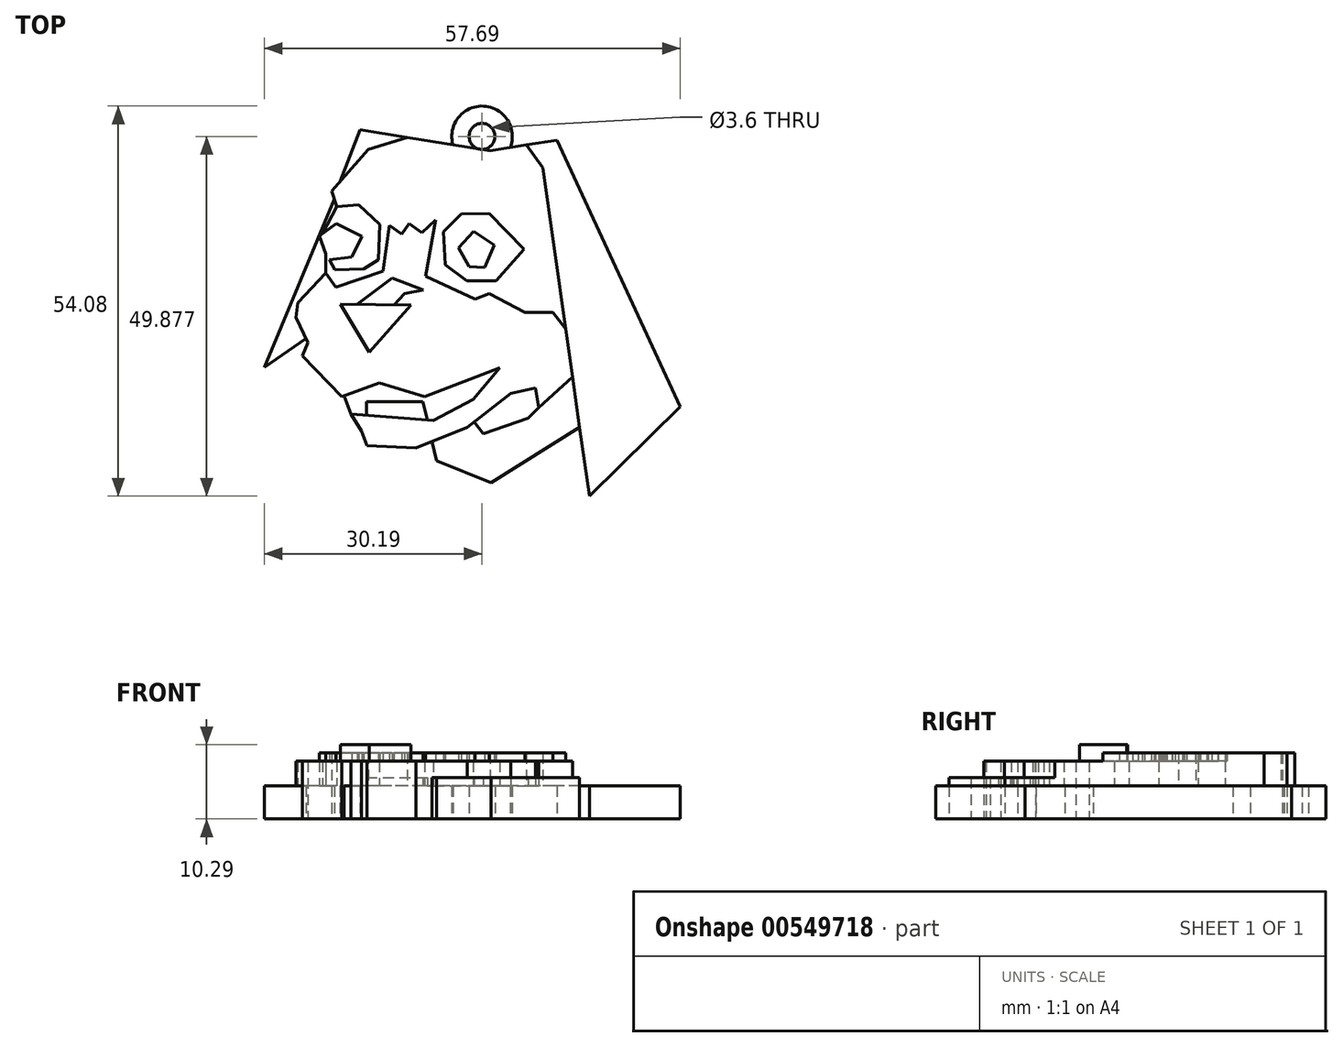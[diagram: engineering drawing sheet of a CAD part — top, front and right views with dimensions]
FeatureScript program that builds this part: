
annotation { "Feature Type Name" : "Feature", "Feature Type Description" : "" }
export const myFeature = defineFeature(function(context is Context, id is Id, definition is map)
    precondition{}
    {
        {
            var Q0;
            Q0=qCreatedBy(makeId("Top.planeOp"),FACE);
            var sketch = newSketch(context, id + "F0", { "sketchPlane" : qUnion([Q0])});
            skLineSegment(sketch, "E0", {"start": v(-28.92, 19.78) * mm, "end": v(-27.96, 16.71) * mm});
            skLineSegment(sketch, "E1", {"start": v(-27.96, 16.71) * mm, "end": v(-23.77, 17.1) * mm});
            skLineSegment(sketch, "E2", {"start": v(-23.77, 17.1) * mm, "end": v(-19.66, 13.35) * mm});
            skLineSegment(sketch, "E3", {"start": v(-19.66, 13.35) * mm, "end": v(-19.93, 6.56) * mm});
            skLineSegment(sketch, "E4", {"start": v(-19.93, 6.56) * mm, "end": v(-22.81, 4.73) * mm});
            skLineSegment(sketch, "E5", {"start": v(-22.81, 4.73) * mm, "end": v(-28.35, 4.56) * mm});
            skLineSegment(sketch, "E6", {"start": v(-28.35, 4.56) * mm, "end": v(-30.1, 7.71) * mm});
            skLineSegment(sketch, "E7", {"start": v(-30.1, 7.71) * mm, "end": v(-30.1, 3.95) * mm});
            skLineSegment(sketch, "E8", {"start": v(-30.1, 7.71) * mm, "end": v(-31.36, 11.09) * mm});
            skLineSegment(sketch, "E9", {"start": v(-31.36, 11.09) * mm, "end": v(-28.1, 13.47) * mm});
            skLineSegment(sketch, "E10", {"start": v(-28.1, 13.47) * mm, "end": v(-23.11, 10.99) * mm});
            skLineSegment(sketch, "E11", {"start": v(-23.11, 10.99) * mm, "end": v(-25.06, 7.08) * mm});
            skLineSegment(sketch, "E12", {"start": v(-25.06, 7.08) * mm, "end": v(-29.42, 6.49) * mm});
            skLineSegment(sketch, "E13", {"start": v(-27.96, 16.71) * mm, "end": v(-30.7, 11.57) * mm});
            skLineSegment(sketch, "E14", {"start": v(-28.44, 18.25) * mm, "end": v(-41.92, -14.16) * mm});
            skLineSegment(sketch, "E15", {"start": v(-41.92, -14.16) * mm, "end": v(-33.9, -8.63) * mm});
            skLineSegment(sketch, "E16", {"start": v(-33.9, -8.63) * mm, "end": v(-35.81, -4.56) * mm});
            skLineSegment(sketch, "E17", {"start": v(-35.81, -4.56) * mm, "end": v(-35.46, -1.8) * mm});
            skLineSegment(sketch, "E18", {"start": v(-35.46, -1.8) * mm, "end": v(-30.1, 3.95) * mm});
            skLineSegment(sketch, "E19", {"start": v(-30.1, 3.95) * mm, "end": v(-28.12, 1.24) * mm});
            skLineSegment(sketch, "E20", {"start": v(-28.12, 1.24) * mm, "end": v(-19.08, 4.3) * mm});
            skLineSegment(sketch, "E21", {"start": v(-19.08, 4.3) * mm, "end": v(-17.81, 13.18) * mm});
            skLineSegment(sketch, "E22", {"start": v(-17.81, 13.18) * mm, "end": v(-15.44, 11.49) * mm});
            skLineSegment(sketch, "E23", {"start": v(-15.44, 11.49) * mm, "end": v(-14, 13.5) * mm});
            skLineSegment(sketch, "E24", {"start": v(-14, 13.5) * mm, "end": v(-11.55, 11.76) * mm});
            skLineSegment(sketch, "E25", {"start": v(-11.55, 11.76) * mm, "end": v(-8.94, 14.17) * mm});
            skLineSegment(sketch, "E26", {"start": v(-8.94, 14.17) * mm, "end": v(-10.88, 3.37) * mm});
            skLineSegment(sketch, "E27", {"start": v(-10.88, 3.37) * mm, "end": v(-1.34, -1.04) * mm});
            skLineSegment(sketch, "E28", {"start": v(-1.34, -1.04) * mm, "end": v(1.4, 0) * mm});
            skLineSegment(sketch, "E29", {"start": v(1.4, 0) * mm, "end": v(8.24, -3.6) * mm});
            skLineSegment(sketch, "E30", {"start": v(8.24, -3.6) * mm, "end": v(13.64, -3.6) * mm});
            skLineSegment(sketch, "E31", {"start": v(13.64, -3.6) * mm, "end": v(16.12, -6.8) * mm});
            skLineSegment(sketch, "E32", {"start": v(11.71, 24.26) * mm, "end": v(20.68, -38.98) * mm});
            skLineSegment(sketch, "E33", {"start": v(20.68, -38.98) * mm, "end": v(38.19, -21.8) * mm});
            skLineSegment(sketch, "E34", {"start": v(38.19, -21.8) * mm, "end": v(14.47, 29.55) * mm});
            skLineSegment(sketch, "E35", {"start": v(14.47, 29.55) * mm, "end": v(1.52, 27.5) * mm});
            skLineSegment(sketch, "E36", {"start": v(4.12, 27.08) * mm, "end": v(-23.44, 31.57) * mm});
            skLineSegment(sketch, "E37", {"start": v(-23.44, 31.57) * mm, "end": v(-27.48, 21.27) * mm});
            skLineSegment(sketch, "E38", {"start": v(-28.92, 19.78) * mm, "end": v(-21.91, 27.77) * mm});
            skLineSegment(sketch, "E39", {"start": v(-21.91, 27.77) * mm, "end": v(-14.43, 30.1) * mm});
            skLineSegment(sketch, "E40", {"start": v(7.07, 24.85) * mm, "end": v(11.71, 24.26) * mm});
            skLineSegment(sketch, "E41", {"start": v(-7.46, 11.9) * mm, "end": v(-3.96, 15.32) * mm});
            skLineSegment(sketch, "E42", {"start": v(-3.96, 15.32) * mm, "end": v(1.35, 15.44) * mm});
            skLineSegment(sketch, "E43", {"start": v(1.35, 15.44) * mm, "end": v(8.1, 8.52) * mm});
            skLineSegment(sketch, "E44", {"start": v(8.1, 8.52) * mm, "end": v(2.67, 2.5) * mm});
            skLineSegment(sketch, "E45", {"start": v(2.67, 2.5) * mm, "end": v(-2.9, 2.5) * mm});
            skLineSegment(sketch, "E46", {"start": v(-2.9, 2.5) * mm, "end": v(-7.12, 5.55) * mm});
            skLineSegment(sketch, "E47", {"start": v(-7.12, 5.55) * mm, "end": v(-7.46, 11.9) * mm});
            skLineSegment(sketch, "E48", {"start": v(-4.5, 8.85) * mm, "end": v(-1.65, 12) * mm});
            skLineSegment(sketch, "E49", {"start": v(-1.65, 12) * mm, "end": v(2.34, 9.35) * mm});
            skLineSegment(sketch, "E50", {"start": v(2.34, 9.35) * mm, "end": v(0.52, 5) * mm});
            skLineSegment(sketch, "E51", {"start": v(0.52, 5) * mm, "end": v(-2.48, 5.22) * mm});
            skLineSegment(sketch, "E52", {"start": v(-2.48, 5.22) * mm, "end": v(-4.5, 8.85) * mm});
            skLineSegment(sketch, "E53", {"start": v(-32.42, -6.74) * mm, "end": v(-34.61, -11.98) * mm});
            skLineSegment(sketch, "E54", {"start": v(-34.61, -11.98) * mm, "end": v(-26.99, -19.8) * mm});
            skLineSegment(sketch, "E55", {"start": v(-26.99, -19.8) * mm, "end": v(-19.76, -17.15) * mm});
            skLineSegment(sketch, "E56", {"start": v(-19.76, -17.15) * mm, "end": v(-11.02, -19.87) * mm});
            skLineSegment(sketch, "E57", {"start": v(-11.02, -19.87) * mm, "end": v(3.38, -14.27) * mm});
            skLineSegment(sketch, "E58", {"start": v(3.38, -14.27) * mm, "end": v(-1.71, -20.33) * mm});
            skLineSegment(sketch, "E59", {"start": v(-1.71, -20.33) * mm, "end": v(-9.37, -24.45) * mm});
            skLineSegment(sketch, "E60", {"start": v(-9.37, -24.45) * mm, "end": v(-25.28, -23.17) * mm});
            skLineSegment(sketch, "E61", {"start": v(-25.28, -23.17) * mm, "end": v(-26.57, -19.65) * mm});
            skLineSegment(sketch, "E62", {"start": v(-22.25, -23.41) * mm, "end": v(-22.25, -20.84) * mm});
            skLineSegment(sketch, "E63", {"start": v(-22.25, -20.84) * mm, "end": v(-11.39, -20.84) * mm});
            skLineSegment(sketch, "E64", {"start": v(-11.39, -20.84) * mm, "end": v(-10.5, -24.36) * mm});
            skLineSegment(sketch, "E65", {"start": v(-25.28, -23.17) * mm, "end": v(-23.24, -26.44) * mm});
            skLineSegment(sketch, "E66", {"start": v(-23.24, -26.44) * mm, "end": v(-22.2, -29.25) * mm});
            skLineSegment(sketch, "E67", {"start": v(-22.2, -29.25) * mm, "end": v(-12.7, -29.74) * mm});
            skLineSegment(sketch, "E68", {"start": v(-12.7, -29.74) * mm, "end": v(-2.87, -25.74) * mm});
            skLineSegment(sketch, "E69", {"start": v(-2.87, -25.74) * mm, "end": v(5.56, -19.21) * mm});
            skLineSegment(sketch, "E70", {"start": v(5.56, -19.21) * mm, "end": v(10.24, -12.1) * mm});
            skLineSegment(sketch, "E71", {"start": v(5.56, -19.21) * mm, "end": v(10.25, -18.17) * mm});
            skLineSegment(sketch, "E72", {"start": v(10.25, -18.17) * mm, "end": v(10.88, -21.95) * mm});
            skLineSegment(sketch, "E73", {"start": v(10.88, -21.95) * mm, "end": v(8.92, -23.96) * mm});
            skLineSegment(sketch, "E74", {"start": v(8.92, -23.96) * mm, "end": v(0.28, -26.95) * mm});
            skLineSegment(sketch, "E75", {"start": v(0.28, -26.95) * mm, "end": v(-1.48, -24.66) * mm});
            skLineSegment(sketch, "E76", {"start": v(10.88, -21.95) * mm, "end": v(17.42, -16.03) * mm});
            skLineSegment(sketch, "E77", {"start": v(-9.63, -28.5) * mm, "end": v(-8.76, -32.21) * mm});
            skLineSegment(sketch, "E78", {"start": v(-8.76, -32.21) * mm, "end": v(1.74, -36.41) * mm});
            skLineSegment(sketch, "E79", {"start": v(1.74, -36.41) * mm, "end": v(18.8, -25.7) * mm});
            skLineSegment(sketch, "E80", {"start": v(-21.73, -11.3) * mm, "end": v(-13.7, -2.22) * mm});
            skLineSegment(sketch, "E81", {"start": v(-13.7, -2.22) * mm, "end": v(-27.3, -2) * mm});
            skLineSegment(sketch, "E82", {"start": v(-27.3, -2) * mm, "end": v(-21.73, -11.3) * mm});
            skLineSegment(sketch, "E83", {"start": v(-17.31, 3.04) * mm, "end": v(-24, -2.06) * mm});
            skLineSegment(sketch, "E84", {"start": v(-17.31, 3.04) * mm, "end": v(-11.32, 0.74) * mm});
            skLineSegment(sketch, "E85", {"start": v(-11.32, 0.74) * mm, "end": v(-14.94, 0) * mm});
            skLineSegment(sketch, "E86", {"start": v(-14.94, 0) * mm, "end": v(-16.95, -2.17) * mm});
            skLineSegment(sketch, "E87", {"start": v(-33.9, -8.63) * mm, "end": v(-33.54, -9.41) * mm});
            skLineSegment(sketch, "E88", {"start": v(11.71, 24.26) * mm, "end": v(8.56, 28.61) * mm});
            skSolve(sketch);
        }
        {
            var Q0;
            {var subQ0=sQuery(id+"F0.wireOp",EDGE,"E33");Q0=makeQuery(id+"F0.imprint","IMPRINT",FACE,{"disambiguationData":[TD([[makeQuery(id+"F0.imprint","IMPRINT",EDGE,{"derivedFrom":subQ0}),1.0]])]});}
            var Q1;
            {var subQ3=sQuery(id+"F0.wireOp",EDGE,"E39");Q1=makeQuery(id+"F0.imprint","IMPRINT",FACE,{"disambiguationData":[TD([[makeQuery(id+"F0.imprint","IMPRINT",EDGE,{"derivedFrom":subQ3}),1.0]])]});}
            var Q2;
            Q2=makeQuery(id+"F0.imprint","IMPRINT",FACE,{"disambiguationData":[TD([[makeQuery(id+"F0.imprint","IMPRINT",EDGE,{"derivedFrom":sQuery(id+"F0.wireOp",EDGE,"E7")}),-1.0]])]});
            var Q3;
            {var subQ0=sQuery(id+"F0.wireOp",EDGE,"E1");Q3=makeQuery(id+"F0.imprint","IMPRINT",FACE,{"disambiguationData":[TD([[makeQuery(id+"F0.imprint","IMPRINT",EDGE,{"derivedFrom":subQ0}),1.0]])]});}
            var Q4;
            Q4=makeQuery(id+"F0.imprint","IMPRINT",FACE,{"disambiguationData":[TD([[makeQuery(id+"F0.imprint","IMPRINT",EDGE,{"derivedFrom":sQuery(id+"F0.wireOp",EDGE,"E1")}),-1.0]])]});
            var Q5;
            {var subQ3=sQuery(id+"F0.wireOp",EDGE,"E8");Q5=makeQuery(id+"F0.imprint","IMPRINT",FACE,{"disambiguationData":[TD([[makeQuery(id+"F0.imprint","IMPRINT",EDGE,{"derivedFrom":subQ3}),-1.0]])]});}
            var Q6;
            Q6=makeQuery(id+"F0.imprint","IMPRINT",FACE,{"disambiguationData":[TD([[makeQuery(id+"F0.imprint","IMPRINT",EDGE,{"derivedFrom":sQuery(id+"F0.wireOp",EDGE,"E48")}),-1.0]])]});
            var Q7;
            Q7=makeQuery(id+"F0.imprint","IMPRINT",FACE,{"disambiguationData":[TD([[makeQuery(id+"F0.imprint","IMPRINT",EDGE,{"derivedFrom":sQuery(id+"F0.wireOp",EDGE,"E41")}),-1.0]])]});
            var Q8;
            Q8=makeQuery(id+"F0.imprint","IMPRINT",FACE,{"disambiguationData":[TD([[makeQuery(id+"F0.imprint","IMPRINT",EDGE,{"derivedFrom":sQuery(id+"F0.wireOp",EDGE,"E16")}),-1.0]])]});
            var Q9;
            {var subQ4=sQuery(id+"F0.wireOp",EDGE,"E80");Q9=makeQuery(id+"F0.imprint","IMPRINT",FACE,{"disambiguationData":[TD([[makeQuery(id+"F0.imprint","IMPRINT",EDGE,{"derivedFrom":subQ4}),1.0]])]});}
            var Q10;
            {var subQ0=sQuery(id+"F0.wireOp",EDGE,"E83");Q10=makeQuery(id+"F0.imprint","IMPRINT",FACE,{"disambiguationData":[TD([[makeQuery(id+"F0.imprint","IMPRINT",EDGE,{"derivedFrom":subQ0}),1.0]])]});}
            var Q11;
            {var subQ5=sQuery(id+"F0.wireOp",EDGE,"E56");Q11=makeQuery(id+"F0.imprint","IMPRINT",FACE,{"disambiguationData":[TD([[makeQuery(id+"F0.imprint","IMPRINT",EDGE,{"derivedFrom":subQ5}),-1.0]])]});}
            var Q12;
            {var subQ0=sQuery(id+"F0.wireOp",EDGE,"E62");Q12=makeQuery(id+"F0.imprint","IMPRINT",FACE,{"disambiguationData":[TD([[makeQuery(id+"F0.imprint","IMPRINT",EDGE,{"derivedFrom":subQ0}),-1.0]])]});}
            var Q13;
            {var subQ0=sQuery(id+"F0.wireOp",EDGE,"E71");Q13=makeQuery(id+"F0.imprint","IMPRINT",FACE,{"disambiguationData":[TD([[makeQuery(id+"F0.imprint","IMPRINT",EDGE,{"derivedFrom":subQ0}),-1.0]])]});}
            var Q14;
            Q14=makeQuery(id+"F0.imprint","IMPRINT",FACE,{"disambiguationData":[TD([[makeQuery(id+"F0.imprint","IMPRINT",EDGE,{"derivedFrom":sQuery(id+"F0.wireOp",EDGE,"E73")}),1.0]])]});
            extrude(context, id + "F1", {"entities" : qUnion([Q0, Q1, Q2, Q3, Q4, Q5, Q6, Q7, Q8, Q9, Q10, Q11, Q12, Q13, Q14]), "depth" : 6.35 * mm, "offsetDistance" : 25.4 * mm});
        }
        {
            var Q0;
            Q0=makeQuery(id+"F0.imprint","IMPRINT",FACE,{"disambiguationData":[TD([[makeQuery(id+"F0.imprint","IMPRINT",EDGE,{"derivedFrom":sQuery(id+"F0.wireOp",EDGE,"E16")}),-1.0]])]});
            var Q1;
            {var subQ0=sQuery(id+"F0.wireOp",EDGE,"E1");Q1=makeQuery(id+"F0.imprint","IMPRINT",FACE,{"disambiguationData":[TD([[makeQuery(id+"F0.imprint","IMPRINT",EDGE,{"derivedFrom":subQ0}),1.0]])]});}
            var Q2;
            {var subQ0=sQuery(id+"F0.wireOp",EDGE,"E62");Q2=makeQuery(id+"F0.imprint","IMPRINT",FACE,{"disambiguationData":[TD([[makeQuery(id+"F0.imprint","IMPRINT",EDGE,{"derivedFrom":subQ0}),-1.0]])]});}
            var Q3;
            {var subQ3=sQuery(id+"F0.wireOp",EDGE,"E8");Q3=makeQuery(id+"F0.imprint","IMPRINT",FACE,{"disambiguationData":[TD([[makeQuery(id+"F0.imprint","IMPRINT",EDGE,{"derivedFrom":subQ3}),-1.0]])]});}
            var Q4;
            Q4=makeQuery(id+"F0.imprint","IMPRINT",FACE,{"disambiguationData":[TD([[makeQuery(id+"F0.imprint","IMPRINT",EDGE,{"derivedFrom":sQuery(id+"F0.wireOp",EDGE,"E48")}),-1.0]])]});
            var Q5;
            {var subQ0=sQuery(id+"F0.wireOp",EDGE,"E83");Q5=makeQuery(id+"F0.imprint","IMPRINT",FACE,{"disambiguationData":[TD([[makeQuery(id+"F0.imprint","IMPRINT",EDGE,{"derivedFrom":subQ0}),1.0]])]});}
            var Q6;
            {var subQ4=sQuery(id+"F0.wireOp",EDGE,"E80");Q6=makeQuery(id+"F0.imprint","IMPRINT",FACE,{"disambiguationData":[TD([[makeQuery(id+"F0.imprint","IMPRINT",EDGE,{"derivedFrom":subQ4}),1.0]])]});}
            var Q7;
            Q7=makeQuery(id+"F0.imprint","IMPRINT",FACE,{"disambiguationData":[TD([[makeQuery(id+"F0.imprint","IMPRINT",EDGE,{"derivedFrom":sQuery(id+"F0.wireOp",EDGE,"E73")}),1.0]])]});
            extrude(context, id + "F2", {"entities" : qUnion([Q0, Q1, Q2, Q3, Q4, Q5, Q6, Q7]), "operationType" : NewBodyOperationType.ADD, "depth" : 7.94 * mm, "offsetDistance" : 25.4 * mm});
        }
        {
            var Q0;
            Q0=makeQuery(id+"F0.imprint","IMPRINT",FACE,{"disambiguationData":[TD([[makeQuery(id+"F0.imprint","IMPRINT",EDGE,{"derivedFrom":sQuery(id+"F0.wireOp",EDGE,"E16")}),-1.0]])]});
            var Q1;
            {var subQ4=sQuery(id+"F0.wireOp",EDGE,"E80");Q1=makeQuery(id+"F0.imprint","IMPRINT",FACE,{"disambiguationData":[TD([[makeQuery(id+"F0.imprint","IMPRINT",EDGE,{"derivedFrom":subQ4}),1.0]])]});}
            var Q2;
            {var subQ0=sQuery(id+"F0.wireOp",EDGE,"E83");Q2=makeQuery(id+"F0.imprint","IMPRINT",FACE,{"disambiguationData":[TD([[makeQuery(id+"F0.imprint","IMPRINT",EDGE,{"derivedFrom":subQ0}),1.0]])]});}
            var Q3;
            {var subQ0=sQuery(id+"F0.wireOp",EDGE,"E1");Q3=makeQuery(id+"F0.imprint","IMPRINT",FACE,{"disambiguationData":[TD([[makeQuery(id+"F0.imprint","IMPRINT",EDGE,{"derivedFrom":subQ0}),1.0]])]});}
            var Q4;
            {var subQ3=sQuery(id+"F0.wireOp",EDGE,"E8");Q4=makeQuery(id+"F0.imprint","IMPRINT",FACE,{"disambiguationData":[TD([[makeQuery(id+"F0.imprint","IMPRINT",EDGE,{"derivedFrom":subQ3}),-1.0]])]});}
            var Q5;
            Q5=makeQuery(id+"F0.imprint","IMPRINT",FACE,{"disambiguationData":[TD([[makeQuery(id+"F0.imprint","IMPRINT",EDGE,{"derivedFrom":sQuery(id+"F0.wireOp",EDGE,"E1")}),-1.0]])]});
            var Q6;
            Q6=makeQuery(id+"F0.imprint","IMPRINT",FACE,{"disambiguationData":[TD([[makeQuery(id+"F0.imprint","IMPRINT",EDGE,{"derivedFrom":sQuery(id+"F0.wireOp",EDGE,"E48")}),-1.0]])]});
            var Q7;
            Q7=makeQuery(id+"F0.imprint","IMPRINT",FACE,{"disambiguationData":[TD([[makeQuery(id+"F0.imprint","IMPRINT",EDGE,{"derivedFrom":sQuery(id+"F0.wireOp",EDGE,"E41")}),-1.0]])]});
            extrude(context, id + "F3", {"entities" : qUnion([Q0, Q1, Q2, Q3, Q4, Q5, Q6, Q7]), "operationType" : NewBodyOperationType.ADD, "depth" : 9.52 * mm, "offsetDistance" : 25.4 * mm});
        }
        {
            var Q0;
            Q0=makeQuery(id+"F0.imprint","IMPRINT",FACE,{"disambiguationData":[TD([[makeQuery(id+"F0.imprint","IMPRINT",EDGE,{"derivedFrom":sQuery(id+"F0.wireOp",EDGE,"E16")}),-1.0]])]});
            var Q1;
            {var subQ4=sQuery(id+"F0.wireOp",EDGE,"E80");Q1=makeQuery(id+"F0.imprint","IMPRINT",FACE,{"disambiguationData":[TD([[makeQuery(id+"F0.imprint","IMPRINT",EDGE,{"derivedFrom":subQ4}),1.0]])]});}
            var Q2;
            {var subQ0=sQuery(id+"F0.wireOp",EDGE,"E83");Q2=makeQuery(id+"F0.imprint","IMPRINT",FACE,{"disambiguationData":[TD([[makeQuery(id+"F0.imprint","IMPRINT",EDGE,{"derivedFrom":subQ0}),1.0]])]});}
            var Q3;
            {var subQ0=sQuery(id+"F0.wireOp",EDGE,"E1");Q3=makeQuery(id+"F0.imprint","IMPRINT",FACE,{"disambiguationData":[TD([[makeQuery(id+"F0.imprint","IMPRINT",EDGE,{"derivedFrom":subQ0}),1.0]])]});}
            var Q4;
            {var subQ3=sQuery(id+"F0.wireOp",EDGE,"E8");Q4=makeQuery(id+"F0.imprint","IMPRINT",FACE,{"disambiguationData":[TD([[makeQuery(id+"F0.imprint","IMPRINT",EDGE,{"derivedFrom":subQ3}),-1.0]])]});}
            var Q5;
            Q5=makeQuery(id+"F0.imprint","IMPRINT",FACE,{"disambiguationData":[TD([[makeQuery(id+"F0.imprint","IMPRINT",EDGE,{"derivedFrom":sQuery(id+"F0.wireOp",EDGE,"E48")}),-1.0]])]});
            extrude(context, id + "F4", {"entities" : qUnion([Q0, Q1, Q2, Q3, Q4, Q5]), "operationType" : NewBodyOperationType.ADD, "depth" : 11.1 * mm, "offsetDistance" : 25.4 * mm});
        }
        {
            var Q0;
            {var subQ0=sQuery(id+"F0.wireOp",EDGE,"E1");Q0=makeQuery(id+"F0.imprint","IMPRINT",FACE,{"disambiguationData":[TD([[makeQuery(id+"F0.imprint","IMPRINT",EDGE,{"derivedFrom":subQ0}),1.0]])]});}
            var Q1;
            {var subQ0=sQuery(id+"F0.wireOp",EDGE,"E83");Q1=makeQuery(id+"F0.imprint","IMPRINT",FACE,{"disambiguationData":[TD([[makeQuery(id+"F0.imprint","IMPRINT",EDGE,{"derivedFrom":subQ0}),1.0]])]});}
            var Q2;
            {var subQ4=sQuery(id+"F0.wireOp",EDGE,"E80");Q2=makeQuery(id+"F0.imprint","IMPRINT",FACE,{"disambiguationData":[TD([[makeQuery(id+"F0.imprint","IMPRINT",EDGE,{"derivedFrom":subQ4}),1.0]])]});}
            extrude(context, id + "F5", {"entities" : qUnion([Q0, Q1, Q2]), "operationType" : NewBodyOperationType.ADD, "depth" : 12.7 * mm, "offsetDistance" : 25.4 * mm});
        }
        {
            var Q0;
            {var subQ4=sQuery(id+"F0.wireOp",EDGE,"E80");Q0=makeQuery(id+"F0.imprint","IMPRINT",FACE,{"disambiguationData":[TD([[makeQuery(id+"F0.imprint","IMPRINT",EDGE,{"derivedFrom":subQ4}),1.0]])]});}
            extrude(context, id + "F6", {"entities" : qUnion([Q0]), "operationType" : NewBodyOperationType.ADD, "depth" : 14.29 * mm, "offsetDistance" : 25.4 * mm});
        }
        {
            var Q0;
            {var subQ0=sQuery(id+"F0.wireOp",EDGE,"E9");var subQ1=sQuery(id+"F0.wireOp",EDGE,"E8");var subQ2=sQuery(id+"F0.wireOp",EDGE,"E7");var subQ3=sQuery(id+"F0.wireOp",EDGE,"E6");var subQ4=sQuery(id+"F0.wireOp",EDGE,"E10");var subQ5=sQuery(id+"F0.wireOp",EDGE,"E11");var subQ6=sQuery(id+"F0.wireOp",EDGE,"E12");Q0=makeQuery(id+"F5.boolean.opBoolean","SPLIT",FACE,{"disambiguationData":[TD([makeQuery(id+"F2.opExtrude","SWEPT_FACE",FACE,{"disambiguationData":[OSD([subQ1])]})])],"derivedFrom":makeQuery(id+"F4.opExtrude","CAP_FACE",FACE,{"disambiguationData":[OSD([sQuery(id+"F0.wireOp",EDGE,"E0"),sQuery(id+"F0.wireOp",EDGE,"E1"),sQuery(id+"F0.wireOp",EDGE,"E2"),sQuery(id+"F0.wireOp",EDGE,"E3"),sQuery(id+"F0.wireOp",EDGE,"E4"),sQuery(id+"F0.wireOp",EDGE,"E5"),subQ3,subQ2,subQ1,subQ0,subQ4,subQ5,subQ6,sQuery(id+"F0.wireOp",EDGE,"E16"),sQuery(id+"F0.wireOp",EDGE,"E17"),sQuery(id+"F0.wireOp",EDGE,"E18"),sQuery(id+"F0.wireOp",EDGE,"E32"),sQuery(id+"F0.wireOp",EDGE,"E35"),sQuery(id+"F0.wireOp",EDGE,"E36"),sQuery(id+"F0.wireOp",EDGE,"E38"),sQuery(id+"F0.wireOp",EDGE,"E39"),sQuery(id+"F0.wireOp",EDGE,"E41"),sQuery(id+"F0.wireOp",EDGE,"E42"),sQuery(id+"F0.wireOp",EDGE,"E43"),sQuery(id+"F0.wireOp",EDGE,"E44"),sQuery(id+"F0.wireOp",EDGE,"E45"),sQuery(id+"F0.wireOp",EDGE,"E46"),sQuery(id+"F0.wireOp",EDGE,"E47"),sQuery(id+"F0.wireOp",EDGE,"E53"),sQuery(id+"F0.wireOp",EDGE,"E54"),sQuery(id+"F0.wireOp",EDGE,"E55"),sQuery(id+"F0.wireOp",EDGE,"E56"),sQuery(id+"F0.wireOp",EDGE,"E57"),sQuery(id+"F0.wireOp",EDGE,"E58"),sQuery(id+"F0.wireOp",EDGE,"E59"),sQuery(id+"F0.wireOp",EDGE,"E60"),sQuery(id+"F0.wireOp",EDGE,"E65"),sQuery(id+"F0.wireOp",EDGE,"E66"),sQuery(id+"F0.wireOp",EDGE,"E67"),sQuery(id+"F0.wireOp",EDGE,"E68"),sQuery(id+"F0.wireOp",EDGE,"E69"),sQuery(id+"F0.wireOp",EDGE,"E71"),sQuery(id+"F0.wireOp",EDGE,"E72"),sQuery(id+"F0.wireOp",EDGE,"E76"),sQuery(id+"F0.wireOp",EDGE,"E87"),sQuery(id+"F0.wireOp",EDGE,"E88")])],"isStart":false})});}
            var Q1;
            Q1=makeQuery(id+"F4.opExtrude","CAP_FACE",FACE,{"disambiguationData":[OSD([sQuery(id+"F0.wireOp",EDGE,"E48"),sQuery(id+"F0.wireOp",EDGE,"E49"),sQuery(id+"F0.wireOp",EDGE,"E50"),sQuery(id+"F0.wireOp",EDGE,"E51"),sQuery(id+"F0.wireOp",EDGE,"E52")])],"isStart":false});
            var Q2;
            Q2=makeQuery(id+"F5.opExtrude","CAP_FACE",FACE,{"disambiguationData":[OSD([sQuery(id+"F0.wireOp",EDGE,"E80"),sQuery(id+"F0.wireOp",EDGE,"E81"),sQuery(id+"F0.wireOp",EDGE,"E82"),sQuery(id+"F0.wireOp",EDGE,"E83"),sQuery(id+"F0.wireOp",EDGE,"E84"),sQuery(id+"F0.wireOp",EDGE,"E85"),sQuery(id+"F0.wireOp",EDGE,"E86")])],"isStart":false});
            extrude(context, id + "F7", {"entities" : qUnion([Q0, Q1]), "operationType" : NewBodyOperationType.ADD, "endBound" : BoundingType.UP_TO_SURFACE, "depth" : 25.4 * mm, "endBoundEntityFace" : qUnion([Q2]), "offsetDistance" : 25.4 * mm});
        }
        {
            var Q0;
            {var subQ0=sQuery(id+"F0.wireOp",EDGE,"E0");var subQ1=sQuery(id+"F0.wireOp",EDGE,"E13");var subQ2=sQuery(id+"F0.wireOp",EDGE,"E9");Q0=makeQuery(id+"F4.boolean.opBoolean","SPLIT",FACE,{"disambiguationData":[TD([makeQuery(id+"F1.opExtrude","SWEPT_FACE",FACE,{"disambiguationData":[OSD([subQ0])]})])],"derivedFrom":makeQuery(id+"F3.opExtrude","CAP_FACE",FACE,{"disambiguationData":[OSD([subQ0,sQuery(id+"F0.wireOp",EDGE,"E7"),sQuery(id+"F0.wireOp",EDGE,"E8"),subQ2,subQ1,sQuery(id+"F0.wireOp",EDGE,"E16"),sQuery(id+"F0.wireOp",EDGE,"E17"),sQuery(id+"F0.wireOp",EDGE,"E18"),sQuery(id+"F0.wireOp",EDGE,"E32"),sQuery(id+"F0.wireOp",EDGE,"E35"),sQuery(id+"F0.wireOp",EDGE,"E36"),sQuery(id+"F0.wireOp",EDGE,"E38"),sQuery(id+"F0.wireOp",EDGE,"E39"),sQuery(id+"F0.wireOp",EDGE,"E53"),sQuery(id+"F0.wireOp",EDGE,"E54"),sQuery(id+"F0.wireOp",EDGE,"E55"),sQuery(id+"F0.wireOp",EDGE,"E56"),sQuery(id+"F0.wireOp",EDGE,"E57"),sQuery(id+"F0.wireOp",EDGE,"E58"),sQuery(id+"F0.wireOp",EDGE,"E59"),sQuery(id+"F0.wireOp",EDGE,"E60"),sQuery(id+"F0.wireOp",EDGE,"E65"),sQuery(id+"F0.wireOp",EDGE,"E66"),sQuery(id+"F0.wireOp",EDGE,"E67"),sQuery(id+"F0.wireOp",EDGE,"E68"),sQuery(id+"F0.wireOp",EDGE,"E69"),sQuery(id+"F0.wireOp",EDGE,"E71"),sQuery(id+"F0.wireOp",EDGE,"E72"),sQuery(id+"F0.wireOp",EDGE,"E76"),sQuery(id+"F0.wireOp",EDGE,"E87"),sQuery(id+"F0.wireOp",EDGE,"E88")])],"isStart":false})});}
            var Q1;
            Q1=makeQuery(id+"F4.boolean.opBoolean","SPLIT",FACE,{"disambiguationData":[TD([makeQuery(id+"F4.opExtrude","SWEPT_FACE",FACE,{"disambiguationData":[OSD([sQuery(id+"F0.wireOp",EDGE,"E41")])]})])],"derivedFrom":makeQuery(id+"F3.opExtrude","CAP_FACE",FACE,{"disambiguationData":[OSD([sQuery(id+"F0.wireOp",EDGE,"E0"),sQuery(id+"F0.wireOp",EDGE,"E7"),sQuery(id+"F0.wireOp",EDGE,"E8"),sQuery(id+"F0.wireOp",EDGE,"E9"),sQuery(id+"F0.wireOp",EDGE,"E13"),sQuery(id+"F0.wireOp",EDGE,"E16"),sQuery(id+"F0.wireOp",EDGE,"E17"),sQuery(id+"F0.wireOp",EDGE,"E18"),sQuery(id+"F0.wireOp",EDGE,"E32"),sQuery(id+"F0.wireOp",EDGE,"E35"),sQuery(id+"F0.wireOp",EDGE,"E36"),sQuery(id+"F0.wireOp",EDGE,"E38"),sQuery(id+"F0.wireOp",EDGE,"E39"),sQuery(id+"F0.wireOp",EDGE,"E53"),sQuery(id+"F0.wireOp",EDGE,"E54"),sQuery(id+"F0.wireOp",EDGE,"E55"),sQuery(id+"F0.wireOp",EDGE,"E56"),sQuery(id+"F0.wireOp",EDGE,"E57"),sQuery(id+"F0.wireOp",EDGE,"E58"),sQuery(id+"F0.wireOp",EDGE,"E59"),sQuery(id+"F0.wireOp",EDGE,"E60"),sQuery(id+"F0.wireOp",EDGE,"E65"),sQuery(id+"F0.wireOp",EDGE,"E66"),sQuery(id+"F0.wireOp",EDGE,"E67"),sQuery(id+"F0.wireOp",EDGE,"E68"),sQuery(id+"F0.wireOp",EDGE,"E69"),sQuery(id+"F0.wireOp",EDGE,"E71"),sQuery(id+"F0.wireOp",EDGE,"E72"),sQuery(id+"F0.wireOp",EDGE,"E76"),sQuery(id+"F0.wireOp",EDGE,"E87"),sQuery(id+"F0.wireOp",EDGE,"E88")])],"isStart":false})});
            var Q2;
            {var subQ0=sQuery(id+"F0.wireOp",EDGE,"E68");var subQ1=sQuery(id+"F0.wireOp",EDGE,"E54");var subQ2=sQuery(id+"F0.wireOp",EDGE,"E67");var subQ3=sQuery(id+"F0.wireOp",EDGE,"E53");var subQ4=sQuery(id+"F0.wireOp",EDGE,"E66");var subQ5=sQuery(id+"F0.wireOp",EDGE,"E65");var subQ6=sQuery(id+"F0.wireOp",EDGE,"E60");var subQ7=sQuery(id+"F0.wireOp",EDGE,"E59");var subQ8=sQuery(id+"F0.wireOp",EDGE,"E7");var subQ9=sQuery(id+"F0.wireOp",EDGE,"E58");var subQ10=sQuery(id+"F0.wireOp",EDGE,"E57");var subQ11=sQuery(id+"F0.wireOp",EDGE,"E56");var subQ12=sQuery(id+"F0.wireOp",EDGE,"E55");var subQ13=sQuery(id+"F0.wireOp",EDGE,"E32");var subQ14=sQuery(id+"F0.wireOp",EDGE,"E18");var subQ15=sQuery(id+"F0.wireOp",EDGE,"E17");var subQ16=sQuery(id+"F0.wireOp",EDGE,"E87");var subQ17=sQuery(id+"F0.wireOp",EDGE,"E16");var subQ18=sQuery(id+"F0.wireOp",EDGE,"E72");var subQ19=sQuery(id+"F0.wireOp",EDGE,"E71");var subQ20=sQuery(id+"F0.wireOp",EDGE,"E69");var subQ21=sQuery(id+"F0.wireOp",EDGE,"E76");Q2=makeQuery(id+"F5.boolean.opBoolean","SPLIT",FACE,{"disambiguationData":[TD([makeQuery(id+"F1.opExtrude","SWEPT_FACE",FACE,{"disambiguationData":[OSD([subQ3])]})])],"derivedFrom":makeQuery(id+"F4.opExtrude","CAP_FACE",FACE,{"disambiguationData":[OSD([sQuery(id+"F0.wireOp",EDGE,"E0"),sQuery(id+"F0.wireOp",EDGE,"E1"),sQuery(id+"F0.wireOp",EDGE,"E2"),sQuery(id+"F0.wireOp",EDGE,"E3"),sQuery(id+"F0.wireOp",EDGE,"E4"),sQuery(id+"F0.wireOp",EDGE,"E5"),sQuery(id+"F0.wireOp",EDGE,"E6"),subQ8,sQuery(id+"F0.wireOp",EDGE,"E8"),sQuery(id+"F0.wireOp",EDGE,"E9"),sQuery(id+"F0.wireOp",EDGE,"E10"),sQuery(id+"F0.wireOp",EDGE,"E11"),sQuery(id+"F0.wireOp",EDGE,"E12"),subQ17,subQ15,subQ14,subQ13,sQuery(id+"F0.wireOp",EDGE,"E35"),sQuery(id+"F0.wireOp",EDGE,"E36"),sQuery(id+"F0.wireOp",EDGE,"E38"),sQuery(id+"F0.wireOp",EDGE,"E39"),sQuery(id+"F0.wireOp",EDGE,"E41"),sQuery(id+"F0.wireOp",EDGE,"E42"),sQuery(id+"F0.wireOp",EDGE,"E43"),sQuery(id+"F0.wireOp",EDGE,"E44"),sQuery(id+"F0.wireOp",EDGE,"E45"),sQuery(id+"F0.wireOp",EDGE,"E46"),sQuery(id+"F0.wireOp",EDGE,"E47"),subQ3,subQ1,subQ12,subQ11,subQ10,subQ9,subQ7,subQ6,subQ5,subQ4,subQ2,subQ0,subQ20,subQ19,subQ18,subQ21,subQ16,sQuery(id+"F0.wireOp",EDGE,"E88")])],"isStart":false})});}
            extrude(context, id + "F8", {"entities" : qUnion([Q0, Q1]), "operationType" : NewBodyOperationType.ADD, "endBound" : BoundingType.UP_TO_SURFACE, "depth" : 25.4 * mm, "endBoundEntityFace" : qUnion([Q2]), "offsetDistance" : 25.4 * mm});
        }
        {
            var Q0;
            Q0=makeQuery(id+"F1.opExtrude","SWEPT_BODY",BODY,{"disambiguationData":[OSD([sQuery(id+"F0.wireOp",EDGE,"E0"),sQuery(id+"F0.wireOp",EDGE,"E14"),sQuery(id+"F0.wireOp",EDGE,"E15"),sQuery(id+"F0.wireOp",EDGE,"E32"),sQuery(id+"F0.wireOp",EDGE,"E33"),sQuery(id+"F0.wireOp",EDGE,"E34"),sQuery(id+"F0.wireOp",EDGE,"E35"),sQuery(id+"F0.wireOp",EDGE,"E36"),sQuery(id+"F0.wireOp",EDGE,"E37"),sQuery(id+"F0.wireOp",EDGE,"E38"),sQuery(id+"F0.wireOp",EDGE,"E53"),sQuery(id+"F0.wireOp",EDGE,"E54"),sQuery(id+"F0.wireOp",EDGE,"E55"),sQuery(id+"F0.wireOp",EDGE,"E61"),sQuery(id+"F0.wireOp",EDGE,"E65"),sQuery(id+"F0.wireOp",EDGE,"E66"),sQuery(id+"F0.wireOp",EDGE,"E67"),sQuery(id+"F0.wireOp",EDGE,"E68"),sQuery(id+"F0.wireOp",EDGE,"E77"),sQuery(id+"F0.wireOp",EDGE,"E78"),sQuery(id+"F0.wireOp",EDGE,"E79"),sQuery(id+"F0.wireOp",EDGE,"E87")])]});
            var Q1;
            Q1=qCreatedBy(makeId("Origin.pointOp"),VERTEX);
            var Q2;
            Q2=qCreatedBy(makeId("Origin.pointOp"),VERTEX);
            transform(context, id + "F9", {"entities" : qUnion([Q0]), "transformType" : TransformType.SCALE_UNIFORMLY, "scale" : 0.72, "scalePoint" : qUnion([Q2]), "makeCopy" : false});
        }
        {
            var Q0;
            Q0=qCreatedBy(makeId("Top.planeOp"),FACE);
            var sketch = newSketch(context, id + "F10", { "sketchPlane" : qUnion([Q0])});
            skLineSegment(sketch, "E89.0.0", {"start": v(-16.88, 22.73) * mm, "end": v(1.1, 19.8) * mm});
            skLineSegment(sketch, "E89.0.1", {"start": v(1.1, 19.8) * mm, "end": v(10.42, 21.28) * mm});
            skLineSegment(sketch, "E89.0.2", {"start": v(10.42, 21.28) * mm, "end": v(27.5, -15.7) * mm});
            skLineSegment(sketch, "E89.0.3", {"start": v(27.5, -15.7) * mm, "end": v(14.9, -28.07) * mm});
            skLineSegment(sketch, "E89.0.4", {"start": v(14.9, -28.07) * mm, "end": v(13.54, -18.51) * mm});
            skLineSegment(sketch, "E89.0.5", {"start": v(13.54, -18.51) * mm, "end": v(1.26, -26.22) * mm});
            skLineSegment(sketch, "E89.0.6", {"start": v(1.26, -26.22) * mm, "end": v(-6.31, -23.2) * mm});
            skLineSegment(sketch, "E89.0.7", {"start": v(-6.31, -23.2) * mm, "end": v(-6.94, -20.52) * mm});
            skLineSegment(sketch, "E89.0.8", {"start": v(-6.94, -20.52) * mm, "end": v(-9.14, -21.42) * mm});
            skLineSegment(sketch, "E89.0.9", {"start": v(-9.14, -21.42) * mm, "end": v(-15.99, -21.07) * mm});
            skLineSegment(sketch, "E89.0.10", {"start": v(-15.99, -21.07) * mm, "end": v(-16.74, -19.04) * mm});
            skLineSegment(sketch, "E89.0.11", {"start": v(-16.74, -19.04) * mm, "end": v(-18.2, -16.68) * mm});
            skLineSegment(sketch, "E89.0.12", {"start": v(-18.2, -16.68) * mm, "end": v(-19.14, -14.15) * mm});
            skLineSegment(sketch, "E89.0.13", {"start": v(-19.14, -14.15) * mm, "end": v(-19.44, -14.26) * mm});
            skLineSegment(sketch, "E89.0.14", {"start": v(-19.44, -14.26) * mm, "end": v(-24.93, -8.63) * mm});
            skLineSegment(sketch, "E89.0.15", {"start": v(-24.93, -8.63) * mm, "end": v(-24.15, -6.78) * mm});
            skLineSegment(sketch, "E89.0.16", {"start": v(-24.15, -6.78) * mm, "end": v(-24.42, -6.21) * mm});
            skLineSegment(sketch, "E89.0.17", {"start": v(-24.42, -6.21) * mm, "end": v(-30.2, -10.2) * mm});
            skLineSegment(sketch, "E89.0.18", {"start": v(-30.2, -10.2) * mm, "end": v(-20.48, 13.14) * mm});
            skLineSegment(sketch, "E89.0.19", {"start": v(-20.48, 13.14) * mm, "end": v(-20.83, 14.25) * mm});
            skLineSegment(sketch, "E89.0.20", {"start": v(-20.83, 14.25) * mm, "end": v(-19.72, 15.51) * mm});
            skLineSegment(sketch, "E89.0.21", {"start": v(-19.72, 15.51) * mm, "end": v(-16.88, 22.73) * mm});
            skCircle(sketch, "E90", {"center": v(0, 21.8) * mm, "radius": 1.8 * mm});
            skCircle(sketch, "E91", {"center": v(0, 21.8) * mm, "radius": 4.2 * mm});
            skSolve(sketch);
        }
        {
            var Q0;
            {var subQ0=sQuery(id+"F10.wireOp",EDGE,"E91");var subQ1=sQuery(id+"F10.wireOp",EDGE,"E89.0.0");var subQ2=makeQuery(id+"F10.imprint","INTERSECT",VERTEX,{"derivedFrom":[subQ1,subQ0]});Q0=makeQuery(id+"F10.imprint","IMPRINT",FACE,{"disambiguationData":[TD([[makeQuery(id+"F10.imprint","IMPRINT",EDGE,{"disambiguationData":[TD([[subQ2,-1.0]])],"derivedFrom":subQ1}),-1.0]])]});}
            var Q1;
            {var subQ0=sQuery(id+"F10.wireOp",EDGE,"E90");Q1=makeQuery(id+"F10.imprint","IMPRINT",FACE,{"disambiguationData":[TD([[makeQuery(id+"F10.imprint","IMPRINT",EDGE,{"derivedFrom":subQ0}),-1.0]])]});}
            var Q2;
            {var subQ0=sQuery(id+"F0.wireOp",EDGE,"E36");var subQ1=sQuery(id+"F0.wireOp",EDGE,"E38");var subQ2=sQuery(id+"F0.wireOp",EDGE,"E37");Q2=makeQuery(id+"F2.boolean.opBoolean","SPLIT",FACE,{"disambiguationData":[TD([makeQuery(id+"F1.opExtrude","SWEPT_FACE",FACE,{"disambiguationData":[OSD([subQ0])]})])],"derivedFrom":makeQuery(id+"F1.opExtrude","CAP_FACE",FACE,{"disambiguationData":[OSD([sQuery(id+"F0.wireOp",EDGE,"E0"),sQuery(id+"F0.wireOp",EDGE,"E14"),sQuery(id+"F0.wireOp",EDGE,"E15"),sQuery(id+"F0.wireOp",EDGE,"E32"),sQuery(id+"F0.wireOp",EDGE,"E33"),sQuery(id+"F0.wireOp",EDGE,"E34"),sQuery(id+"F0.wireOp",EDGE,"E35"),subQ0,subQ2,subQ1,sQuery(id+"F0.wireOp",EDGE,"E53"),sQuery(id+"F0.wireOp",EDGE,"E54"),sQuery(id+"F0.wireOp",EDGE,"E55"),sQuery(id+"F0.wireOp",EDGE,"E61"),sQuery(id+"F0.wireOp",EDGE,"E65"),sQuery(id+"F0.wireOp",EDGE,"E66"),sQuery(id+"F0.wireOp",EDGE,"E67"),sQuery(id+"F0.wireOp",EDGE,"E68"),sQuery(id+"F0.wireOp",EDGE,"E77"),sQuery(id+"F0.wireOp",EDGE,"E78"),sQuery(id+"F0.wireOp",EDGE,"E79"),sQuery(id+"F0.wireOp",EDGE,"E87")])],"isStart":false})});}
            extrude(context, id + "F11", {"entities" : qUnion([Q0, Q1]), "operationType" : NewBodyOperationType.ADD, "endBound" : BoundingType.UP_TO_SURFACE, "depth" : 25.4 * mm, "endBoundEntityFace" : qUnion([Q2]), "offsetDistance" : 25.4 * mm});
        }
    });
